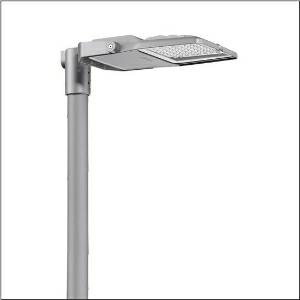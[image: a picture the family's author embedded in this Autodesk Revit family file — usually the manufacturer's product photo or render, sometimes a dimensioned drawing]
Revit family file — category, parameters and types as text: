
# Revit family: floodlight_fl_21_mini___pl64_5xa7776c2e3a_3ffb
name_source: partatom
category: Lighting Fixtures
units: mm (PartAtom-declared; Revit-internal decimal feet)

## family parameters
Cut with Voids When Loaded = No
Host = Face
Light Source = No
Part Type = Normal
Room Calculation Point = No
Round Connector Dimension = Use Diameter
Shared = No

## types (1)
- --- (1 x LED, 11770 lm, 89 W, 3000K)
    Apparent Load = 89 VA
    CIE Flux Codes = 28 80 98 100 100
    Color Rendering = 70
    Color Temperature = 3000K
    Default Elevation = 1800 mm
    Description = Floodlight FL 21 mini, floodlight, primary light control with lens, of PMMA, primary optical cover: protective disc, of toughened safety glass, transparent, light distribution: PL64, light emission: direct distribution, installation type: surface-mounted, LED, High Power LED, rated luminous flux: 11.770lm, luminous efficacy: 132lm/W, light colour: 730, colour temperature: 3000K, control gear: Smart Interface (Zhaga), control: flexible luminous flux parameterisation, time-dependent luminous flux control, constant luminous flux control, overheat protection, pre-setting: logarithmic dimming characteristic, with terminal, 6-pole, mains connection: 220..240V, AC, 50/60Hz, start of lifetime: 89W, end of service life: 94W, reduction: 43W, luminaire housing, of diecast aluminium, powder-coated, Siteco® metallic grey (DB 702S), corrosivity category C5 mid according to DIN EN ISO 12944, suitable for swimming pools, chlorine-resistant, sealing non-destructively replaceable, please order mast flange separately, mast bracket, of steel, galvanised, powder-coated, Siteco® metallic grey (DB 702S), Smart Interface below and above, protection rating (complete): IP66, insulation class (complete): insulation class II (safety insulation), certification: CE, ENEC, VDE, protection symbol: D, impact resistance: IK08, permissible operating ambient temperature: -40..+40°C, permissible operating ambient temperature for outdoor applications: -40..+50°C, standard: DIN EN 12944, LABS conformity tested according to VDMA 24364:2018-05, packaging unit: 1 piece

Light Distribution: PL64
    Height = 70 mm
    Lamp = 1 x LED
    Lamp Light Flux = 11770 lm
    Lamp Power = 89 W
    Lamp count = 1
    Length = 485 mm
    Luminous efficacy = 132 lm/W
    Manufacturer = Siteco
    ModVariant = No
    Model = 5XA7776C2E3A
    Number of Poles = 1
    OnlyDefault = Yes
    Power Factor = 1
    Product Name = Floodlight FL 21 mini | PL64
    Product group = floodlight | pylon annexe
    ProductGroupID = 6200
    Protection Class = Protection class II
    Protection Degree = IP 66
    RLX_Detail_Level = 1
    RLX_Emergency_Light_Flux = 0 lm
    RLX_Emergency_Type = 0
    RLX_Emergency_Type_DB = No
    RlxData = <blob elided: 100973 chars, md5=30503b3f>
    Socket = socket
    Standby Power = 0 W
    System Light Flux = 11770 lm
    System Power = 89 W
    Type Comments = factory setting: luminous flux: 100 % | dim-lin: 254 | 456 mA
    Type Image = l_1007125.jpg
    URL = http://relux.com
    VarID = @adj_165348
    Voltage = 0 V
    Weight = 0.00 kg
    Width = 337 mm

## geometry (parser evidence)
native form markers: Blend x4, Sweep x12
no freeform markers — native parametric forms only
